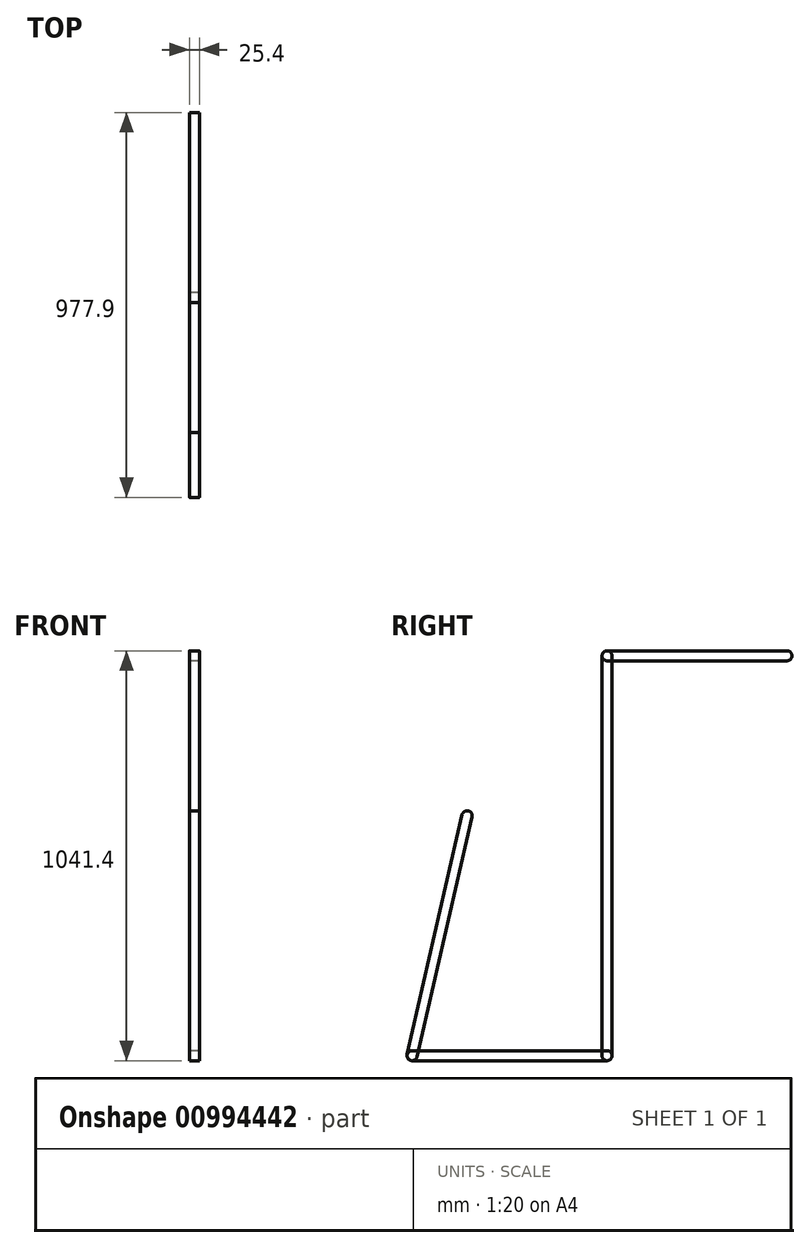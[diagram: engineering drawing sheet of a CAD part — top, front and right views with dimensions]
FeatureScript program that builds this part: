
annotation { "Feature Type Name" : "Feature", "Feature Type Description" : "" }
export const myFeature = defineFeature(function(context is Context, id is Id, definition is map)
    precondition{}
    {
        {
            var Q0;
            Q0=qCreatedBy(makeId("Right.planeOp"),FACE);
            var sketch = newSketch(context, id + "F0", { "sketchPlane" : qUnion([Q0])});
            skLineSegment(sketch, "E0", {"start": v(0, 0) * mm, "end": v(-812.8, 609.6) * mm, "construction": true});
            skLineSegment(sketch, "E1", {"start": v(-812.8, 609.6) * mm, "end": v(-812.8, 0) * mm, "construction": true});
            skLineSegment(sketch, "E2", {"start": v(0, 1016) * mm, "end": v(0, 0) * mm, "construction": true});
            skLineSegment(sketch, "E3", {"start": v(-812.8, 609.6) * mm, "end": v(-355.6, 609.6) * mm, "construction": true});
            skLineSegment(sketch, "E4", {"start": v(0, 1016) * mm, "end": v(457.2, 1016) * mm, "construction": true});
            skLineSegment(sketch, "E5", {"start": v(457.2, 1016) * mm, "end": v(0, 0) * mm, "construction": true});
            skLineSegment(sketch, "E6", {"start": v(-355.6, 609.6) * mm, "end": v(-495.3, 0) * mm, "construction": true});
            skLineSegment(sketch, "E7", {"start": v(-495.3, 0) * mm, "end": v(0, 0) * mm, "construction": true});
            skCircle(sketch, "E8", {"center": v(457.2, 1016) * mm, "radius": 12.7 * mm});
            skCircle(sketch, "E9", {"center": v(0, 1016) * mm, "radius": 12.7 * mm});
            skCircle(sketch, "E10", {"center": v(0, 0) * mm, "radius": 12.7 * mm});
            skCircle(sketch, "E11", {"center": v(-495.3, 0) * mm, "radius": 12.7 * mm});
            skCircle(sketch, "E12", {"center": v(-355.6, 609.6) * mm, "radius": 12.7 * mm});
            skLineSegment(sketch, "E13.0", {"start": v(-367.98, 612.44) * mm, "end": v(-507.68, 2.84) * mm});
            skLineSegment(sketch, "E14.0", {"start": v(-343.22, 606.76) * mm, "end": v(-482.92, -2.84) * mm});
            skLineSegment(sketch, "E15.0", {"start": v(-495.3, -12.7) * mm, "end": v(0, -12.7) * mm});
            skLineSegment(sketch, "E16.0", {"start": v(-495.3, 12.7) * mm, "end": v(0, 12.7) * mm});
            skLineSegment(sketch, "E17.0", {"start": v(0, 1003.3) * mm, "end": v(457.2, 1003.3) * mm});
            skLineSegment(sketch, "E18.0", {"start": v(0, 1028.7) * mm, "end": v(457.2, 1028.7) * mm});
            skLineSegment(sketch, "E19.0", {"start": v(-12.7, 1016) * mm, "end": v(-12.7, 0) * mm});
            skLineSegment(sketch, "E20.0", {"start": v(12.7, 1016) * mm, "end": v(12.7, 0) * mm});
            skSolve(sketch);
        }
        {
            var Q0;
            {var subQ0=sQuery(id+"F0.wireOp",EDGE,"E9");var subQ1=makeQuery(id+"F0.imprint","INTERSECT",VERTEX,{"derivedFrom":[subQ0,sQuery(id+"F0.wireOp",EDGE,"E18.0")]});Q0=makeQuery(id+"F0.imprint","IMPRINT",FACE,{"disambiguationData":[TD([[makeQuery(id+"F0.imprint","IMPRINT",EDGE,{"disambiguationData":[TD([[subQ1,1.0]])],"derivedFrom":subQ0}),1.0]])]});}
            var Q1;
            {var subQ0=sQuery(id+"F0.wireOp",EDGE,"E17.0");var subQ1=sQuery(id+"F0.wireOp",EDGE,"E9");var subQ2=makeQuery(id+"F0.imprint","INTERSECT",VERTEX,{"derivedFrom":[subQ1,subQ0]});Q1=makeQuery(id+"F0.imprint","IMPRINT",FACE,{"disambiguationData":[TD([[makeQuery(id+"F0.imprint","IMPRINT",EDGE,{"disambiguationData":[TD([[subQ2,-1.0]])],"derivedFrom":subQ1}),-1.0]])]});}
            var Q2;
            {var subQ0=sQuery(id+"F0.wireOp",EDGE,"E10");var subQ1=makeQuery(id+"F0.imprint","INTERSECT",VERTEX,{"derivedFrom":[subQ0,sQuery(id+"F0.wireOp",EDGE,"E16.0")]});Q2=makeQuery(id+"F0.imprint","IMPRINT",FACE,{"disambiguationData":[TD([[makeQuery(id+"F0.imprint","IMPRINT",EDGE,{"disambiguationData":[TD([[subQ1,1.0]])],"derivedFrom":subQ0}),1.0]])]});}
            var Q3;
            {var subQ0=sQuery(id+"F0.wireOp",EDGE,"E16.0");var subQ1=sQuery(id+"F0.wireOp",EDGE,"E10");var subQ2=makeQuery(id+"F0.imprint","INTERSECT",VERTEX,{"derivedFrom":[subQ1,subQ0]});Q3=makeQuery(id+"F0.imprint","IMPRINT",FACE,{"disambiguationData":[TD([[makeQuery(id+"F0.imprint","IMPRINT",EDGE,{"disambiguationData":[TD([[subQ2,-1.0]])],"derivedFrom":subQ1}),-1.0]])]});}
            var Q4;
            {var subQ0=sQuery(id+"F0.wireOp",EDGE,"E17.0");var subQ1=sQuery(id+"F0.wireOp",EDGE,"E9");var subQ2=makeQuery(id+"F0.imprint","INTERSECT",VERTEX,{"derivedFrom":[subQ1,subQ0]});Q4=makeQuery(id+"F0.imprint","IMPRINT",FACE,{"disambiguationData":[TD([[makeQuery(id+"F0.imprint","IMPRINT",EDGE,{"disambiguationData":[TD([[subQ2,1.0]])],"derivedFrom":subQ1}),-1.0]])]});}
            extrude(context, id + "F1", {"entities" : qUnion([Q0, Q1, Q2, Q3, Q4]), "depth" : 25.4 * mm, "offsetDistance" : 25.4 * mm});
        }
        {
            var Q0;
            {var subQ5=sQuery(id+"F0.wireOp",EDGE,"E18.0");Q0=makeQuery(id+"F0.imprint","IMPRINT",FACE,{"disambiguationData":[TD([[makeQuery(id+"F0.imprint","IMPRINT",EDGE,{"derivedFrom":subQ5}),-1.0]])]});}
            var Q1;
            {var subQ0=sQuery(id+"F0.wireOp",EDGE,"E8");var subQ1=makeQuery(id+"F0.imprint","INTERSECT",VERTEX,{"derivedFrom":[subQ0,sQuery(id+"F0.wireOp",EDGE,"E17.0")]});Q1=makeQuery(id+"F0.imprint","IMPRINT",FACE,{"disambiguationData":[TD([[makeQuery(id+"F0.imprint","IMPRINT",EDGE,{"disambiguationData":[TD([[subQ1,1.0]])],"derivedFrom":subQ0}),1.0]])]});}
            var Q2;
            {var subQ0=sQuery(id+"F0.wireOp",EDGE,"E9");var subQ1=makeQuery(id+"F0.imprint","INTERSECT",VERTEX,{"derivedFrom":[subQ0,sQuery(id+"F0.wireOp",EDGE,"E18.0")]});Q2=makeQuery(id+"F0.imprint","IMPRINT",FACE,{"disambiguationData":[TD([[makeQuery(id+"F0.imprint","IMPRINT",EDGE,{"disambiguationData":[TD([[subQ1,1.0]])],"derivedFrom":subQ0}),1.0]])]});}
            var Q3;
            {var subQ0=sQuery(id+"F0.wireOp",EDGE,"E17.0");var subQ1=sQuery(id+"F0.wireOp",EDGE,"E9");var subQ2=makeQuery(id+"F0.imprint","INTERSECT",VERTEX,{"derivedFrom":[subQ1,subQ0]});Q3=makeQuery(id+"F0.imprint","IMPRINT",FACE,{"disambiguationData":[TD([[makeQuery(id+"F0.imprint","IMPRINT",EDGE,{"disambiguationData":[TD([[subQ2,-1.0]])],"derivedFrom":subQ1}),-1.0]])]});}
            extrude(context, id + "F2", {"entities" : qUnion([Q0, Q1, Q2, Q3]), "depth" : 25.4 * mm, "offsetDistance" : 25.4 * mm});
        }
        {
            var Q0;
            {var subQ0=sQuery(id+"F0.wireOp",EDGE,"E11");var subQ1=makeQuery(id+"F0.imprint","INTERSECT",VERTEX,{"derivedFrom":[subQ0,sQuery(id+"F0.wireOp",EDGE,"E13.0")]});Q0=makeQuery(id+"F0.imprint","IMPRINT",FACE,{"disambiguationData":[TD([[makeQuery(id+"F0.imprint","IMPRINT",EDGE,{"disambiguationData":[TD([[subQ1,1.0]])],"derivedFrom":subQ0}),1.0]])]});}
            var Q1;
            {var subQ0=sQuery(id+"F0.wireOp",EDGE,"E15.0");Q1=makeQuery(id+"F0.imprint","IMPRINT",FACE,{"disambiguationData":[TD([[makeQuery(id+"F0.imprint","IMPRINT",EDGE,{"derivedFrom":subQ0}),1.0]])]});}
            var Q2;
            {var subQ0=sQuery(id+"F0.wireOp",EDGE,"E14.0");var subQ1=sQuery(id+"F0.wireOp",EDGE,"E11");var subQ2=makeQuery(id+"F0.imprint","INTERSECT",VERTEX,{"derivedFrom":[subQ1,subQ0]});Q2=makeQuery(id+"F0.imprint","IMPRINT",FACE,{"disambiguationData":[TD([[makeQuery(id+"F0.imprint","IMPRINT",EDGE,{"disambiguationData":[TD([[subQ2,-1.0]])],"derivedFrom":subQ1}),-1.0]])]});}
            var Q3;
            {var subQ0=sQuery(id+"F0.wireOp",EDGE,"E16.0");var subQ1=sQuery(id+"F0.wireOp",EDGE,"E10");var subQ2=makeQuery(id+"F0.imprint","INTERSECT",VERTEX,{"derivedFrom":[subQ1,subQ0]});Q3=makeQuery(id+"F0.imprint","IMPRINT",FACE,{"disambiguationData":[TD([[makeQuery(id+"F0.imprint","IMPRINT",EDGE,{"disambiguationData":[TD([[subQ2,-1.0]])],"derivedFrom":subQ1}),-1.0]])]});}
            var Q4;
            {var subQ0=sQuery(id+"F0.wireOp",EDGE,"E10");var subQ1=makeQuery(id+"F0.imprint","INTERSECT",VERTEX,{"derivedFrom":[subQ0,sQuery(id+"F0.wireOp",EDGE,"E16.0")]});Q4=makeQuery(id+"F0.imprint","IMPRINT",FACE,{"disambiguationData":[TD([[makeQuery(id+"F0.imprint","IMPRINT",EDGE,{"disambiguationData":[TD([[subQ1,1.0]])],"derivedFrom":subQ0}),1.0]])]});}
            extrude(context, id + "F3", {"entities" : qUnion([Q0, Q1, Q2, Q3, Q4]), "depth" : 25.4 * mm, "offsetDistance" : 25.4 * mm});
        }
        {
            var Q0;
            {var subQ0=sQuery(id+"F0.wireOp",EDGE,"E11");var subQ1=makeQuery(id+"F0.imprint","INTERSECT",VERTEX,{"derivedFrom":[subQ0,sQuery(id+"F0.wireOp",EDGE,"E13.0")]});Q0=makeQuery(id+"F0.imprint","IMPRINT",FACE,{"disambiguationData":[TD([[makeQuery(id+"F0.imprint","IMPRINT",EDGE,{"disambiguationData":[TD([[subQ1,1.0]])],"derivedFrom":subQ0}),1.0]])]});}
            var Q1;
            {var subQ0=sQuery(id+"F0.wireOp",EDGE,"E14.0");var subQ1=sQuery(id+"F0.wireOp",EDGE,"E11");var subQ2=makeQuery(id+"F0.imprint","INTERSECT",VERTEX,{"derivedFrom":[subQ1,subQ0]});Q1=makeQuery(id+"F0.imprint","IMPRINT",FACE,{"disambiguationData":[TD([[makeQuery(id+"F0.imprint","IMPRINT",EDGE,{"disambiguationData":[TD([[subQ2,-1.0]])],"derivedFrom":subQ1}),-1.0]])]});}
            var Q2;
            {var subQ5=sQuery(id+"F0.wireOp",EDGE,"E13.0");Q2=makeQuery(id+"F0.imprint","IMPRINT",FACE,{"disambiguationData":[TD([[makeQuery(id+"F0.imprint","IMPRINT",EDGE,{"derivedFrom":subQ5}),1.0]])]});}
            var Q3;
            {var subQ0=sQuery(id+"F0.wireOp",EDGE,"E12");var subQ1=makeQuery(id+"F0.imprint","INTERSECT",VERTEX,{"derivedFrom":[subQ0,sQuery(id+"F0.wireOp",EDGE,"E13.0")]});Q3=makeQuery(id+"F0.imprint","IMPRINT",FACE,{"disambiguationData":[TD([[makeQuery(id+"F0.imprint","IMPRINT",EDGE,{"disambiguationData":[TD([[subQ1,-1.0]])],"derivedFrom":subQ0}),1.0]])]});}
            extrude(context, id + "F4", {"entities" : qUnion([Q0, Q1, Q2, Q3]), "depth" : 25.4 * mm, "offsetDistance" : 25.4 * mm});
        }
    });
